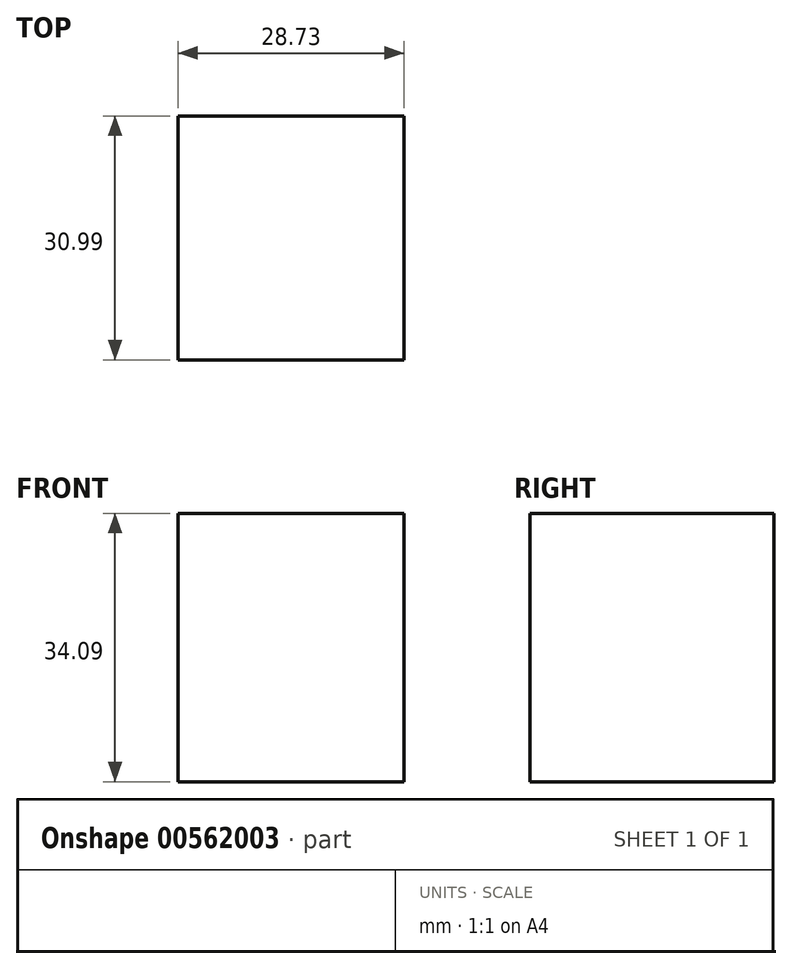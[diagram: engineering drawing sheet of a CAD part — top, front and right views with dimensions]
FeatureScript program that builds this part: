
annotation { "Feature Type Name" : "Feature", "Feature Type Description" : "" }
export const myFeature = defineFeature(function(context is Context, id is Id, definition is map)
    precondition{}
    {
        {
            var Q0;
            Q0=qCreatedBy(makeId("Front.planeOp"),FACE);
            var sketch = newSketch(context, id + "F0", { "sketchPlane" : qUnion([Q0])});
            skLineSegment(sketch, "E0.bottom", {"start": v(-92.14, 22.97) * mm, "end": v(-63.41, 22.97) * mm});
            skLineSegment(sketch, "E0.top", {"start": v(-92.14, -11.12) * mm, "end": v(-63.41, -11.12) * mm});
            skLineSegment(sketch, "E0.left", {"start": v(-92.14, 22.97) * mm, "end": v(-92.14, -11.12) * mm});
            skLineSegment(sketch, "E0.right", {"start": v(-63.41, 22.97) * mm, "end": v(-63.41, -11.12) * mm});
            skLineSegment(sketch, "E1.bottom", {"start": v(-77.77, 22.97) * mm, "end": v(-75.32, 22.97) * mm});
            skLineSegment(sketch, "E1.top", {"start": v(-77.77, 29.58) * mm, "end": v(-75.32, 29.58) * mm});
            skLineSegment(sketch, "E1.left", {"start": v(-77.77, 22.97) * mm, "end": v(-77.77, 29.58) * mm});
            skLineSegment(sketch, "E1.right", {"start": v(-75.32, 22.97) * mm, "end": v(-75.32, 29.58) * mm});
            skSolve(sketch);
        }
        {
            var Q0;
            Q0=makeQuery(id+"F0.imprint","IMPRINT",FACE,{"disambiguationData":[TD([[makeQuery(id+"F0.imprint","IMPRINT",EDGE,{"derivedFrom":sQuery(id+"F0.wireOp",EDGE,"E0.top")}),1.0]])]});
            extrude(context, id + "F1", {"entities" : qUnion([Q0]), "depth" : 30.99 * mm, "offsetDistance" : 25.4 * mm});
        }
    });
